# Revit family: FP_Revit_18_HBD600I_Internal_Blower_90001865A
name_source: partatom
category: Specialty Equipment
revit_build: Autodesk Revit 2018 (Build: 20170223_1515(x64)
units: mm (PartAtom-declared; Revit-internal decimal feet)

## family parameters
Always vertical = Yes
Cut with Voids When Loaded = Yes
OmniClass Number = 23.40.40.00
OmniClass Title = Food Service Equipment and Furnishings
Part Type = Normal
Room Calculation Point = No
Round Connector Dimension = Use Diameter
Shared = No
Work Plane-Based = No

## types (3) — shared parameters
Chassis - Depth = 330 mm  [stored 1.08268 ft]
Chassis - Height = 330 mm  [stored 1.08268 ft]
Chassis - Width = 254 mm
Connector Description - Electrical = 120 V, 60 Hz, 2.8 A
Connector Description - Extraction = 6” (152 mm) round ducting, 600 CFM
Description = Internal Blower
Manufacturer = Fisher & Paykel Appliances
Material - Body = Fisher & Paykel - Grey
Model = HBD600I
Product - Depth = 410 mm  [stored 1.34514 ft]
Product - Height = 365 mm  [stored 1.19751 ft]
Product - Width = 254 mm
URL = www.fisherpaykel.com
Visibility - Clearance Required = Yes

## type names (no varying parameters)
- HBD600I (Outlet Down)
- HBD600I (Outlet Back)
- HBD600I (Outlet Front)

note: [stored X ft] marks values corroborated as IEEE doubles in the binary element streams (Revit-internal decimal feet)

## geometry (parser evidence)
native form markers: Sweep x2
no freeform markers — native parametric forms only
